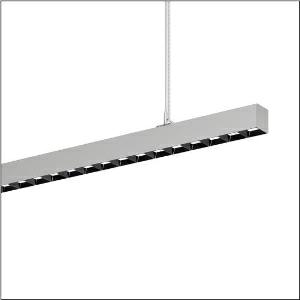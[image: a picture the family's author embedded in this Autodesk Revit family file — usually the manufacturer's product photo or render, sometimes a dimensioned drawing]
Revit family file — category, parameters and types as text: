
# Revit family: silica_r__21_51mx34dc4dsb_5451
name_source: partatom
category: Lighting Fixtures
units: mm (PartAtom-declared; Revit-internal decimal feet)

## family parameters
Cut with Voids When Loaded = No
Host = Face
Light Source = No
Part Type = Normal
Room Calculation Point = No
Round Connector Dimension = Use Diameter
Shared = No

## types (1)
- --- (1 x LED, 19200 lm, 120.3 W, 4000K)
    Apparent Load = 120 VA
    CIE Flux Codes = 74 94 99 56 100
    Color Rendering = 80
    Color Temperature = 4000K
    Default Elevation = 1800 mm
    Description = Silica® 21, office luminaire, primary light control with darklight reflector, of PMMA, black, light emission: direct/indirect distribution, primary light characteristic: asymmetric, installation type: suspended mounting, LED, rated luminous flux: 19.200lm, luminous efficacy: 160lm/W, light colour: 840, colour temperature: 4000K, with terminal, 3+2-pole, max. 2.5mm², mains connection: 220..240V, AC, 50/60Hz, rated input power: 120.3W, luminaire housing, of aluminium, metallic grey (RAL 9006), length: 3.004mm, width: 53mm, height: 53mm, protection rating (complete): IP20, insulation class (complete): insulation class I (protective earthing), certification: CE, permissible operating ambient temperature: 0..+35°C, standard: EN 50419, packaging unit: 1 piece
    Height = 53 mm
    Lamp = 1 x LED
    Lamp Light Flux = 19200 lm
    Lamp Power = 120.3 W
    Lamp count = 1
    Length = 3004 mm
    Luminous efficacy = 160 lm/W
    Manufacturer = Siteco
    ModVariant = No
    Model = 51MX34DC4DSB
    Mounting Place = Ceiling
    Mounting Type = Pendant
    Number of Poles = 1
    OnlyDefault = Yes
    Power Factor = 1
    Product Name = Silica® 21
    Product group = office luminaire | ceiling pendant
    ProductGroupID = 902
    Protection Class = Protection class I
    Protection Degree = IP 20
    RLX_Detail_Level = 1
    RLX_Emergency_Light_Flux = 0 lm
    RLX_Emergency_Type = 0
    RLX_Emergency_Type_DB = No
    RlxData = <blob elided: 66025 chars, md5=ea288fe4>
    Socket = socket
    Standby Power = 0 W
    System Light Flux = 19200 lm
    System Power = 120 W
    Type Comments = factory setting: luminous flux: 100 % | dim-lin: 254 | 418 mA
    Type Image = l_1297751.jpg
    URL = http://relux.com
    VarID = @adj_050579
    Voltage = 0 V
    Weight = 0.00 kg
    Width = 53 mm

## geometry (parser evidence)
native form markers: Blend x4, Sweep x10
no freeform markers — native parametric forms only
